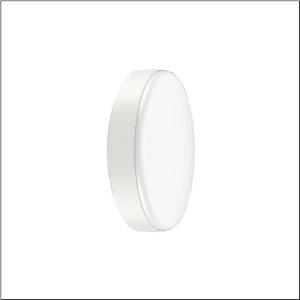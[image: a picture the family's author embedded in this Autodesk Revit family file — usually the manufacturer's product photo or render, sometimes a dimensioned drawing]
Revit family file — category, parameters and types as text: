
# Revit family: rondel_31_51wc10mb44as
name_source: partatom
category: Lighting Fixtures
units: mm (PartAtom-declared; Revit-internal decimal feet)

## family parameters
Cut with Voids When Loaded = No
Host = Face
Light Source = No
Part Type = Normal
Room Calculation Point = No
Round Connector Dimension = Use Diameter
Shared = No

## types (1)
- --- (1 x LED, 4400 lm, 35.5 W, 4000K)
    Apparent Load = 36 VA
    CIE Flux Codes = 44 75 94 94 100
    Color Rendering = 80
    Color Temperature = 4000K
    Default Elevation = 1800 mm
    Description = Rondel 31, wall and ceiling luminaire, primary optical cover: cover, of PC, opal, light emission: direct distribution, primary light characteristic: symmetric, installation type: surface-mounted, LED, rated luminous flux: 4.400lm, luminous efficacy: 124lm/W, light colour: 840, colour temperature: 4000K, with terminal, 3-pole, max. 2.5mm², mains connection: 220..240V, AC, 50/60Hz, rated input power: 35.5W, luminaire housing, of PC, traffic white (RAL 9016), diameter: 480mm, brightness and presence sensor, HF sensor, protection rating (complete): IP65, insulation class (complete): insulation class II (safety insulation), certification: CE, impact resistance: IK10, permissible operating ambient temperature: -20..+40°C, permissible storage temperature: -20..+60°C, packaging unit: 1 piece
    Height = 97 mm
    Lamp = 1 x LED
    Lamp Light Flux = 4400 lm
    Lamp Power = 35.5 W
    Lamp count = 1
    Length = 480 mm
    Luminous efficacy = 124 lm/W
    Manufacturer = Siteco
    ModVariant = No
    Model = 51WC10MB44AS
    Mounting Place = Ceiling
    Mounting Type = Surface mounted
    Number of Poles = 1
    OnlyDefault = Yes
    Power Factor = 1
    Product Name = Rondel 31
    Product group = wall and ceiling luminaire
    ProductGroupID = 301
    Protection Class = Protection class II
    Protection Degree = IP 65
    RLX_Detail_Level = 1
    RLX_Emergency_Light_Flux = 0 lm
    RLX_Emergency_Type = 0
    RLX_Emergency_Type_DB = No
    RlxData = <blob elided: 41469 chars, md5=6814522a>
    Socket = socket
    Standby Power = 0 W
    System Light Flux = 4400 lm
    System Power = 36 W
    Type Comments = factory setting: luminous flux: 100 % | (ON | ON)
    Type Image = l_1007188.jpg
    URL = http://relux.com
    VarID = @adj_083007
    Voltage = 0 V
    Weight = 0.00 kg
    Width = 0 mm  [stored 0 ft]

note: [stored X ft] marks values corroborated as IEEE doubles in the binary element streams (Revit-internal decimal feet)

## geometry (parser evidence)
native form markers: Blend x4, Sweep x11
no freeform markers — native parametric forms only
